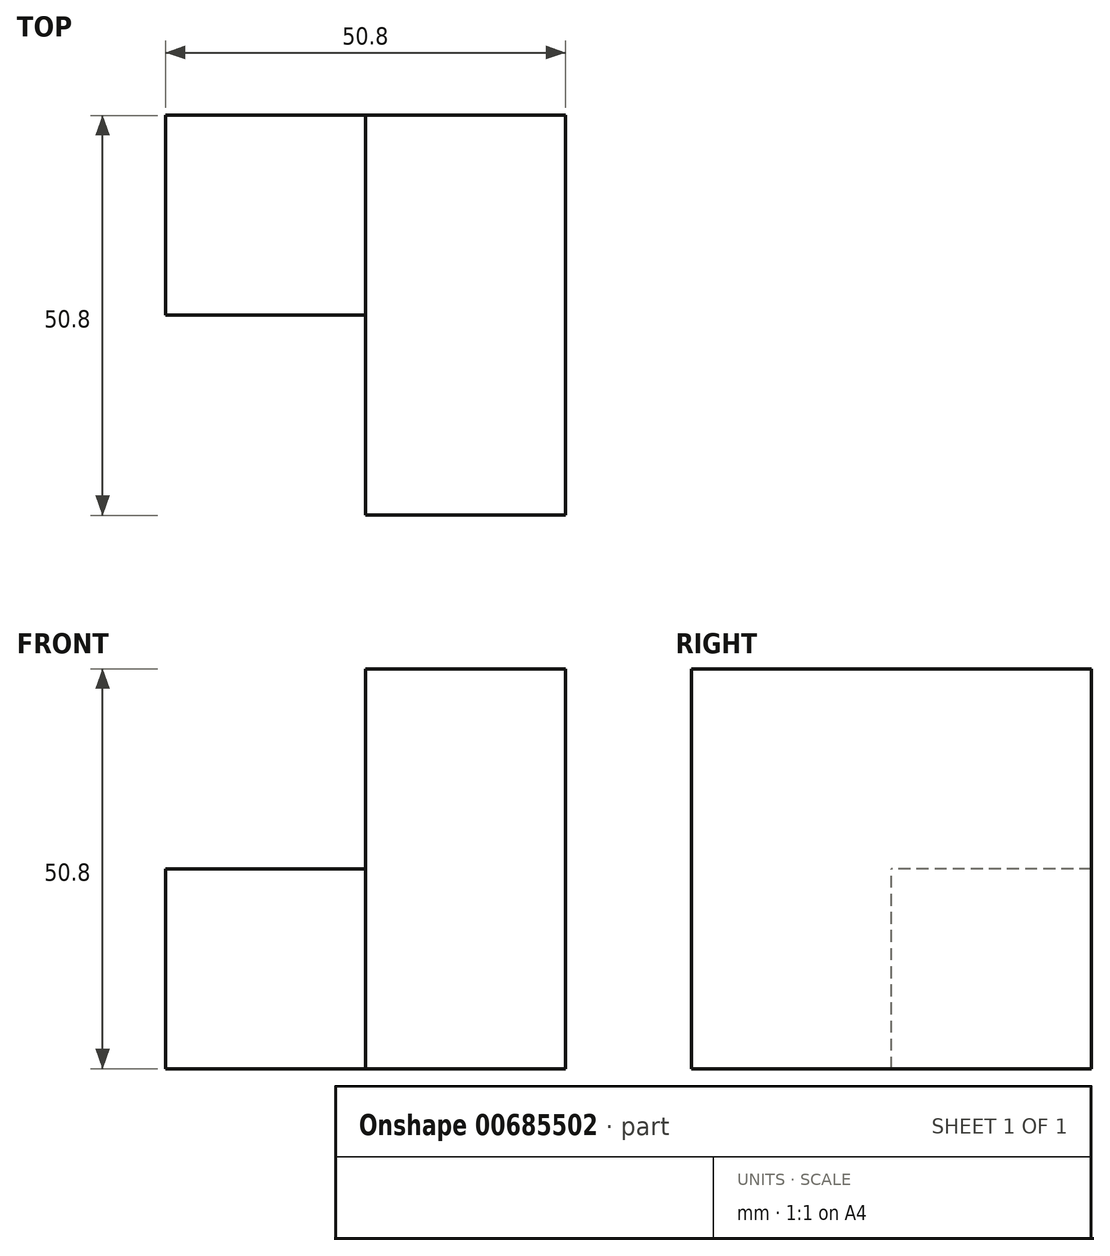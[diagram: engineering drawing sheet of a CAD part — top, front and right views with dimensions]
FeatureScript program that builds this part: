
annotation { "Feature Type Name" : "Feature", "Feature Type Description" : "" }
export const myFeature = defineFeature(function(context is Context, id is Id, definition is map)
    precondition{}
    {
        {
            var Q0;
            Q0=qCreatedBy(makeId("Right.planeOp"),FACE);
            var sketch = newSketch(context, id + "F0", { "sketchPlane" : qUnion([Q0])});
            skLineSegment(sketch, "E0.bottom", {"start": v(2.2, 15.38) * mm, "end": v(-48.6, 15.38) * mm});
            skLineSegment(sketch, "E0.top", {"start": v(2.2, -35.42) * mm, "end": v(-48.6, -35.42) * mm});
            skLineSegment(sketch, "E0.left", {"start": v(2.2, 15.38) * mm, "end": v(2.2, -35.42) * mm});
            skLineSegment(sketch, "E0.right", {"start": v(-48.6, 15.38) * mm, "end": v(-48.6, -35.42) * mm});
            skSolve(sketch);
        }
        {
            var Q0;
            Q0 = qSketchRegion(id + "F0", true);
            extrude(context, id + "F1", {"entities" : qUnion([Q0]), "depth" : 25.4 * mm, "offsetDistance" : 25.4 * mm});
        }
        {
            var Q0;
            Q0=makeQuery(id+"F1.opExtrude","CAP_FACE",FACE,{"disambiguationData":[OSD([sQuery(id+"F0.wireOp",EDGE,"E0.bottom"),sQuery(id+"F0.wireOp",EDGE,"E0.top"),sQuery(id+"F0.wireOp",EDGE,"E0.left"),sQuery(id+"F0.wireOp",EDGE,"E0.right")])],"isStart":true});
            var sketch = newSketch(context, id + "F2", { "sketchPlane" : qUnion([Q0])});
            skLineSegment(sketch, "E1.bottom", {"start": v(-2.2, -35.42) * mm, "end": v(23.2, -35.42) * mm});
            skLineSegment(sketch, "E1.top", {"start": v(-2.2, -10.02) * mm, "end": v(23.2, -10.02) * mm});
            skLineSegment(sketch, "E1.left", {"start": v(-2.2, -35.42) * mm, "end": v(-2.2, -10.02) * mm});
            skLineSegment(sketch, "E1.right", {"start": v(23.2, -35.42) * mm, "end": v(23.2, -10.02) * mm});
            skSolve(sketch);
        }
        {
            var Q0;
            Q0 = qSketchRegion(id + "F2", true);
            extrude(context, id + "F3", {"entities" : qUnion([Q0]), "operationType" : NewBodyOperationType.ADD, "depth" : 25.4 * mm, "offsetDistance" : 25.4 * mm});
        }
    });
